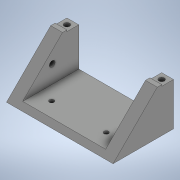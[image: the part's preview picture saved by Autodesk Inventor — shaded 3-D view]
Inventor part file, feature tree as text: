
AUTODESK INVENTOR PART (.ipt)
format: ipt  version: 2020 (Build 240168000, 168)  size: 421,888 bytes
history: native  units: mm
features: other x3, extrude x3, sketch x3
ambient origin geometry x8: Origin, YZ Plane, XZ Plane, XY Plane, X Axis, Y Axis, Z Axis, Center Point
bodies: Solid1 (feature_tree)
feature tree (9):
  other  "VertBody.ipt"
  extrude  "Extrusion26"  Depth=10.0mm TaperAngle=0.0deg
  extrude  "Extrusion27"  Depth=54.185mm TaperAngle=0.0deg
  extrude  "Extrusion28"  [1 undecoded]
  other  "Solid1::VertBody.ipt"
  other  "TaggingFeature1"
  sketch  "Sketch33"  dims[d146=10.0mm d147=41.652mm d148=0.0mm]
  sketch  "Sketch34"  dims[d149=0.0mm d150=0.0mm d151=54.185mm d152=0.0mm]
  sketch  "Sketch35"
note: 1 required parameter value undecoded (feature->parameter linkage not recoverable at this tier; creation-order binding heuristic only, values carry confidence <= 0.55)
